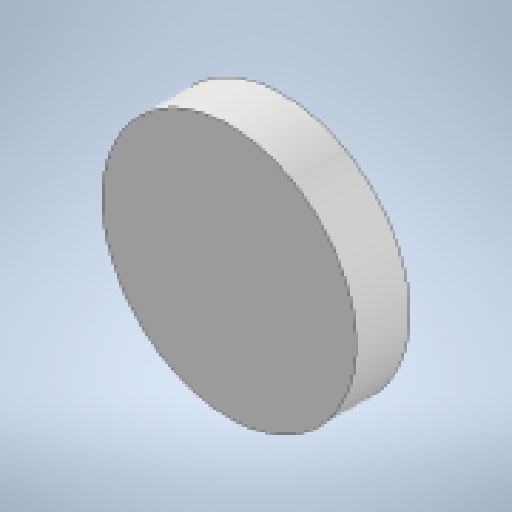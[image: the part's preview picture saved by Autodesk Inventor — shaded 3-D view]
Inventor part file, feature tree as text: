
AUTODESK INVENTOR PART (.ipt)
format: ipt  version: 2023 (Build 270158000, 158)  size: 162,304 bytes
history: native  units: in
note: dims shown in document units (in); Inventor stores cm internally (conversion verified against a paired STEP export)
features: sketch x3, extrude x2, hole x1
ambient origin geometry x8: Origin, YZ Plane, XZ Plane, XY Plane, X Axis, Y Axis, Z Axis, Center Point
bodies: Solid1 (feature_tree)
feature tree (6):
  extrude  "Extrusion1"  Depth=0.1575in TaperAngle=0.0deg
  hole  "Hole1"  [1 undecoded]
  extrude  "Extrusion2"  Depth=0.5906in
  sketch  "Sketch1"  dims[d0=1.1811in d1=0.1575in d2=0.0in]
  sketch  "Sketch2"  dims[d3=0.1378in d4=0.2362in d5=0.2362in d6=0.0787in d7=90.0deg d8=0.2362in d9=0.0in d10=0.7874in]
  sketch  "Sketch4"  dims[d12=0.3937in d13=0.0984in d14=0.3937in d15=0.3937in d16=0.5906in d17=0.0in]
note: 1 required parameter value undecoded (feature->parameter linkage not recoverable at this tier; creation-order binding heuristic only, values carry confidence <= 0.55)
